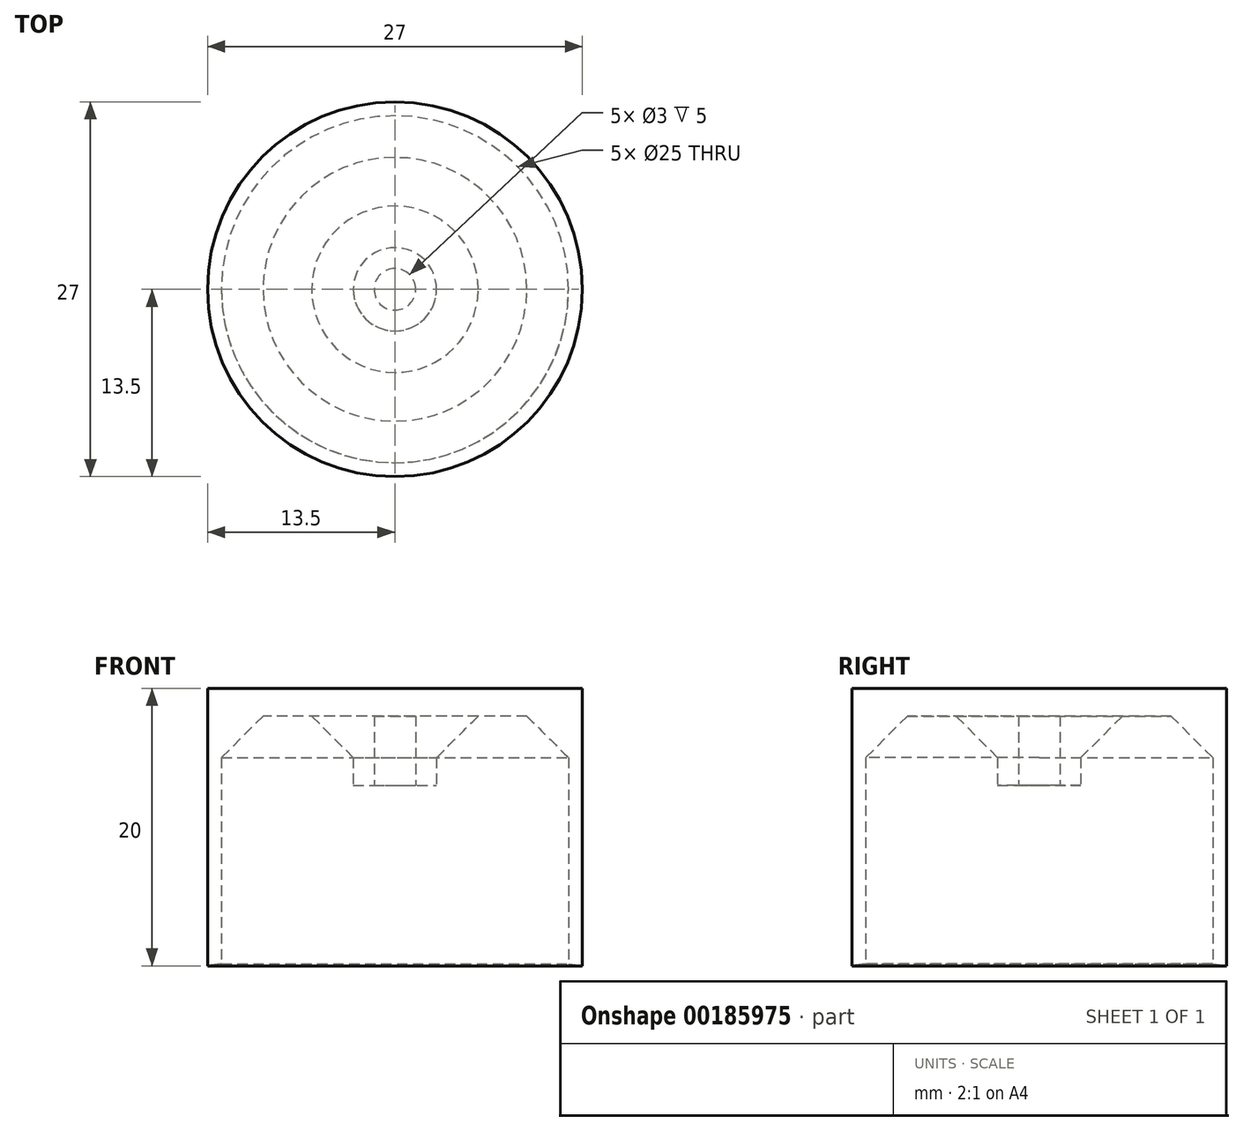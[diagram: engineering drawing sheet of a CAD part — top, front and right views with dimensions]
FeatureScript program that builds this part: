
annotation { "Feature Type Name" : "Feature", "Feature Type Description" : "" }
export const myFeature = defineFeature(function(context is Context, id is Id, definition is map)
    precondition{}
    {
        {
            var Q0;
            Q0=qCreatedBy(makeId("Front.planeOp"),FACE);
            var sketch = newSketch(context, id + "F0", { "sketchPlane" : qUnion([Q0])});
            skLineSegment(sketch, "E0", {"start": v(0, 0) * mm, "end": v(0, 51.61) * mm, "construction": true});
            skLineSegment(sketch, "E1", {"start": v(0, 20) * mm, "end": v(13.5, 20) * mm});
            skLineSegment(sketch, "E2", {"start": v(13.5, 20) * mm, "end": v(13.5, 0) * mm});
            skLineSegment(sketch, "E3", {"start": v(13.5, 0) * mm, "end": v(12.5, 0.14) * mm});
            skLineSegment(sketch, "E4", {"start": v(12.5, 0.14) * mm, "end": v(12.5, 18) * mm});
            skLineSegment(sketch, "E5", {"start": v(12.5, 18) * mm, "end": v(3, 18) * mm});
            skLineSegment(sketch, "E6", {"start": v(3, 18) * mm, "end": v(3, 13) * mm});
            skLineSegment(sketch, "E7", {"start": v(3, 13) * mm, "end": v(1.5, 13) * mm});
            skLineSegment(sketch, "E8", {"start": v(1.5, 13) * mm, "end": v(1.5, 18) * mm});
            skLineSegment(sketch, "E9", {"start": v(1.5, 18) * mm, "end": v(0, 18) * mm});
            skLineSegment(sketch, "E10", {"start": v(0, 18) * mm, "end": v(0, 20) * mm});
            skSolve(sketch);
        }
        {
            var Q0;
            Q0=makeQuery(id+"F0.imprint","IMPRINT",FACE,{"disambiguationData":[TD([[makeQuery(id+"F0.imprint","IMPRINT",EDGE,{"derivedFrom":sQuery(id+"F0.wireOp",EDGE,"E1")}),-1.0]])]});
            var Q1;
            Q1=sQuery(id+"F0.wireOp",EDGE,"E0");
            revolve(context, id + "F1", {"entities" : qUnion([Q0]), "axis" : qUnion([Q1]), "revolveType" : RevolveType.FULL});
        }
        {
            var Q0;
            Q0=makeQuery(id+"F1.opRevolve","SWEPT_EDGE",EDGE,{"disambiguationData":[OSD([sQuery(id+"F0.wireOp",EDGE,"E5"),sQuery(id+"F0.wireOp",EDGE,"E6")])]});
            var Q1;
            Q1=makeQuery(id+"F1.opRevolve","SWEPT_EDGE",EDGE,{"disambiguationData":[OSD([sQuery(id+"F0.wireOp",EDGE,"E4"),sQuery(id+"F0.wireOp",EDGE,"E5")])]});
            chamfer(context, id + "F2", {"entities" : qUnion([Q0, Q1]), "width" : 3 * mm, "tangentPropagation" : true});
        }
    });
